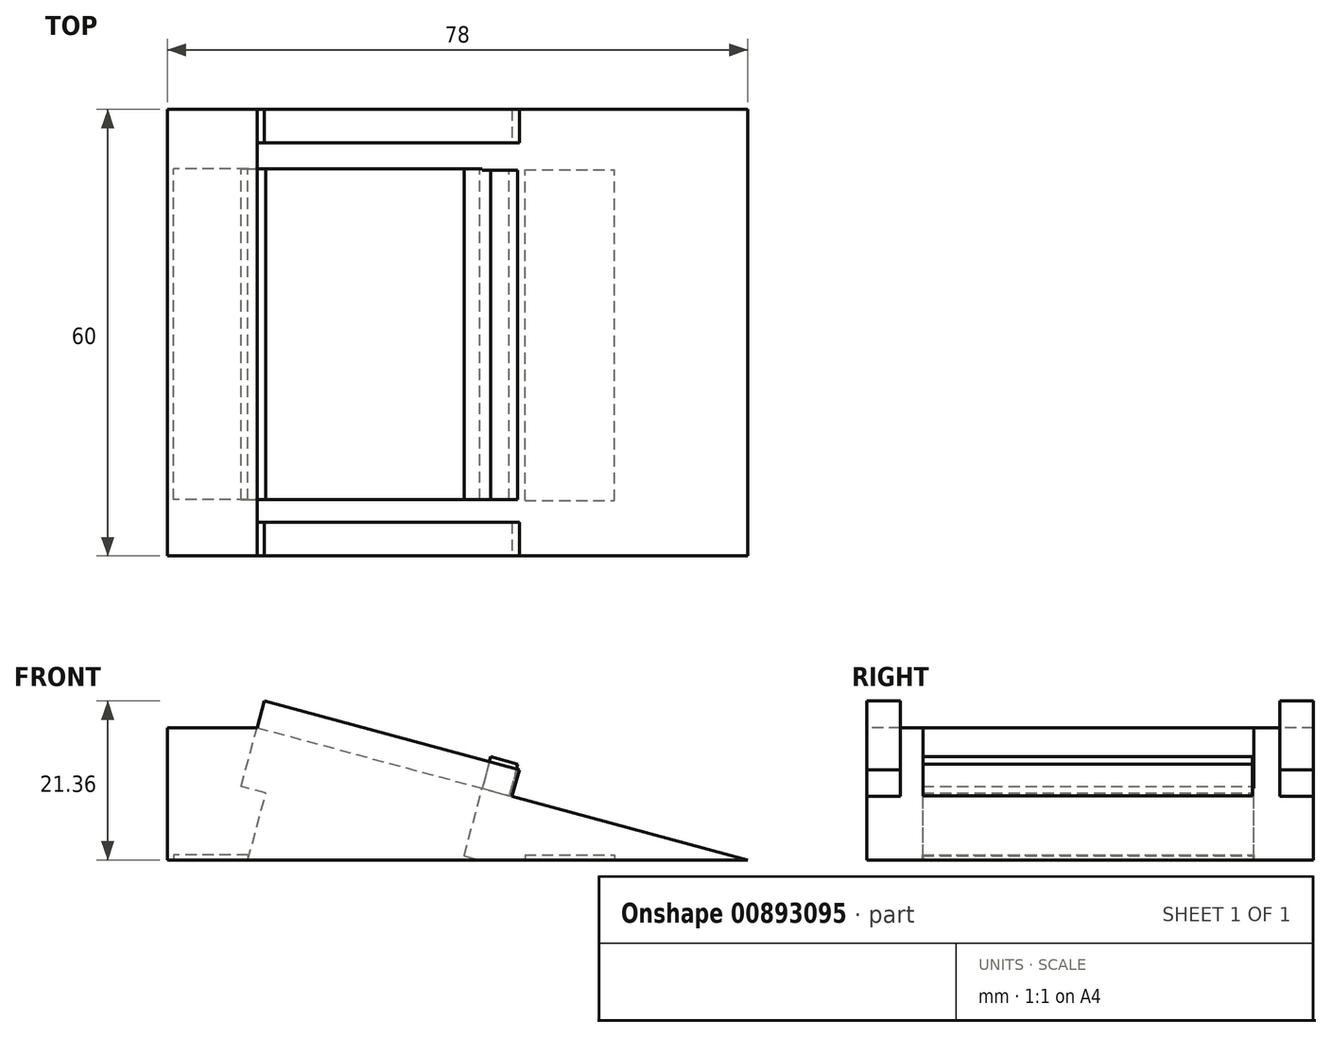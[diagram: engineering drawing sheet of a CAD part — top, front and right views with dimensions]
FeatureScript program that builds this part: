
annotation { "Feature Type Name" : "Feature", "Feature Type Description" : "" }
export const myFeature = defineFeature(function(context is Context, id is Id, definition is map)
    precondition{}
    {
        {
            var Q0;
            Q0=qCreatedBy(makeId("Top.planeOp"),FACE);
            var sketch = newSketch(context, id + "F0", { "sketchPlane" : qUnion([Q0])});
            skLineSegment(sketch, "E0.bottom", {"start": v(-49.5, -60) * mm, "end": v(50.5, -60) * mm});
            skLineSegment(sketch, "E0.top", {"start": v(-49.5, 0) * mm, "end": v(50.5, 0) * mm});
            skLineSegment(sketch, "E0.left", {"start": v(-49.5, -60) * mm, "end": v(-49.5, 0) * mm});
            skLineSegment(sketch, "E0.right", {"start": v(50.5, -60) * mm, "end": v(50.5, 0) * mm});
            skSolve(sketch);
        }
        {
            var Q0;
            Q0=makeQuery(id+"F0.imprint","IMPRINT",FACE,{"disambiguationData":[TD([[makeQuery(id+"F0.imprint","IMPRINT",EDGE,{"derivedFrom":sQuery(id+"F0.wireOp",EDGE,"E0.bottom")}),1.0]])]});
            extrude(context, id + "F1", {"entities" : qUnion([Q0]), "depth" : 31 * mm, "offsetDistance" : 25 * mm});
        }
        {
            var Q0;
            Q0=makeQuery(id+"F1.opExtrude","SWEPT_FACE",FACE,{"disambiguationData":[OSD([sQuery(id+"F0.wireOp",EDGE,"E0.bottom")])]});
            var sketch = newSketch(context, id + "F2", { "sketchPlane" : qUnion([Q0])});
            skLineSegment(sketch, "E1", {"start": v(50.5, 0) * mm, "end": v(-49.5, 26.98) * mm});
            skLineSegment(sketch, "E2", {"start": v(-49.5, 26.98) * mm, "end": v(-49.5, 31) * mm});
            skLineSegment(sketch, "E3", {"start": v(-49.5, 31) * mm, "end": v(50.5, 31) * mm});
            skLineSegment(sketch, "E4", {"start": v(50.5, 31) * mm, "end": v(50.5, 0) * mm});
            skSolve(sketch);
        }
        {
            var Q0;
            Q0 = qSketchRegion(id + "F2", true);
            extrude(context, id + "F3", {"entities" : qUnion([Q0]), "operationType" : NewBodyOperationType.REMOVE, "endBound" : BoundingType.THROUGH_ALL, "oppositeDirection" : true, "depth" : 25 * mm, "offsetDistance" : 25 * mm});
        }
        {
            var Q0;
            Q0=makeQuery(id+"F3.boolean.opBoolean","COPY",FACE,{"derivedFrom":makeQuery(id+"F3.opExtrude","SWEPT_FACE",FACE,{"disambiguationData":[OSD([sQuery(id+"F2.wireOp",EDGE,"E1")])]})});
            var sketch = newSketch(context, id + "F4", { "sketchPlane" : qUnion([Q0])});
            skLineSegment(sketch, "E5.bottom", {"start": v(-16.1, -52.45) * mm, "end": v(14, -52.45) * mm});
            skLineSegment(sketch, "E5.top", {"start": v(-16.1, -8) * mm, "end": v(14, -8) * mm});
            skLineSegment(sketch, "E5.left", {"start": v(-16.1, -52.45) * mm, "end": v(-16.1, -8) * mm});
            skLineSegment(sketch, "E5.right", {"start": v(14, -52.45) * mm, "end": v(14, -8) * mm});
            skSolve(sketch);
        }
        {
            var Q0;
            Q0=makeQuery(id+"F4.imprint","IMPRINT",FACE,{"disambiguationData":[TD([[makeQuery(id+"F4.imprint","IMPRINT",EDGE,{"derivedFrom":sQuery(id+"F4.wireOp",EDGE,"E5.bottom")}),1.0]])]});
            extrude(context, id + "F5", {"entities" : qUnion([Q0]), "operationType" : NewBodyOperationType.REMOVE, "endBound" : BoundingType.THROUGH_ALL, "oppositeDirection" : true, "depth" : 14.7 * mm, "offsetDistance" : 25 * mm});
        }
        {
            var Q0;
            Q0=makeQuery(id+"F3.boolean.opBoolean","COPY",FACE,{"derivedFrom":makeQuery(id+"F3.opExtrude","SWEPT_FACE",FACE,{"disambiguationData":[OSD([sQuery(id+"F2.wireOp",EDGE,"E1")])]})});
            var sketch = newSketch(context, id + "F6", { "sketchPlane" : qUnion([Q0])});
            skLineSegment(sketch, "E6.bottom", {"start": v(-16.1, -52.45) * mm, "end": v(-19.53, -52.45) * mm});
            skLineSegment(sketch, "E6.top", {"start": v(-16.1, -8) * mm, "end": v(-19.53, -8) * mm});
            skLineSegment(sketch, "E6.left", {"start": v(-16.1, -52.45) * mm, "end": v(-16.1, -8) * mm});
            skLineSegment(sketch, "E6.right", {"start": v(-19.53, -52.45) * mm, "end": v(-19.53, -8) * mm});
            skSolve(sketch);
        }
        {
            var Q0;
            Q0 = qSketchRegion(id + "F6", true);
            extrude(context, id + "F7", {"entities" : qUnion([Q0]), "operationType" : NewBodyOperationType.REMOVE, "oppositeDirection" : true, "depth" : 8.2 * mm, "offsetDistance" : 25 * mm});
        }
        {
            var Q0;
            Q0=makeQuery(id+"F5.boolean.opBoolean","COPY",FACE,{"derivedFrom":makeQuery(id+"F5.opExtrude","SWEPT_FACE",FACE,{"disambiguationData":[OSD([sQuery(id+"F4.wireOp",EDGE,"E5.right")])]})});
            extrude(context, id + "F8", {"entities" : qUnion([Q0]), "operationType" : NewBodyOperationType.ADD, "depth" : 2.2 * mm, "offsetDistance" : 25 * mm});
        }
        {
            var Q0;
            Q0=makeQuery(id+"F1.opExtrude","SWEPT_FACE",FACE,{"disambiguationData":[OSD([sQuery(id+"F0.wireOp",EDGE,"E0.left")])]});
            extrude(context, id + "F9", {"entities" : qUnion([Q0]), "operationType" : NewBodyOperationType.REMOVE, "oppositeDirection" : true, "depth" : 22 * mm, "offsetDistance" : 25 * mm});
        }
        {
            var Q0;
            Q0=makeQuery(id+"F8.boolean.opBoolean","MERGE",FACE,{"derivedFrom":[makeQuery(id+"F3.boolean.opBoolean","COPY",FACE,{"derivedFrom":makeQuery(id+"F3.opExtrude","SWEPT_FACE",FACE,{"disambiguationData":[OSD([sQuery(id+"F2.wireOp",EDGE,"E1")])]})}),makeQuery(id+"F8.opExtrude","SWEPT_FACE",FACE,{"disambiguationData":[OSD([sQuery(id+"F4.wireOp",EDGE,"E5.right")])]})]});
            var sketch = newSketch(context, id + "F10", { "sketchPlane" : qUnion([Q0])});
            skLineSegment(sketch, "E7.bottom", {"start": v(11.8, -52.45) * mm, "end": v(15.57, -52.45) * mm});
            skLineSegment(sketch, "E7.top", {"start": v(11.8, -8.16) * mm, "end": v(15.57, -8.16) * mm});
            skLineSegment(sketch, "E7.left", {"start": v(11.8, -52.45) * mm, "end": v(11.8, -8.16) * mm});
            skLineSegment(sketch, "E7.right", {"start": v(15.57, -52.45) * mm, "end": v(15.57, -8.16) * mm});
            skSolve(sketch);
        }
        {
            var Q0;
            Q0=makeQuery(id+"F10.imprint","IMPRINT",FACE,{"disambiguationData":[TD([[makeQuery(id+"F10.imprint","IMPRINT",EDGE,{"derivedFrom":sQuery(id+"F10.wireOp",EDGE,"E7.bottom")}),1.0]])]});
            extrude(context, id + "F11", {"entities" : qUnion([Q0]), "operationType" : NewBodyOperationType.ADD, "depth" : 3.6 * mm, "offsetDistance" : 25 * mm});
        }
        {
            var Q0;
            Q0=makeQuery(id+"F8.boolean.opBoolean","MERGE",FACE,{"derivedFrom":[makeQuery(id+"F3.boolean.opBoolean","COPY",FACE,{"derivedFrom":makeQuery(id+"F3.opExtrude","SWEPT_FACE",FACE,{"disambiguationData":[OSD([sQuery(id+"F2.wireOp",EDGE,"E1")])]})}),makeQuery(id+"F8.opExtrude","SWEPT_FACE",FACE,{"disambiguationData":[OSD([sQuery(id+"F4.wireOp",EDGE,"E5.right")])]})]});
            var sketch = newSketch(context, id + "F12", { "sketchPlane" : qUnion([Q0])});
            skLineSegment(sketch, "E8.bottom", {"start": v(-19.53, 0) * mm, "end": v(15.97, 0) * mm});
            skLineSegment(sketch, "E8.top", {"start": v(-19.53, -4.5) * mm, "end": v(15.97, -4.5) * mm});
            skLineSegment(sketch, "E8.left", {"start": v(-19.53, 0) * mm, "end": v(-19.53, -4.5) * mm});
            skLineSegment(sketch, "E8.right", {"start": v(15.97, 0) * mm, "end": v(15.97, -4.5) * mm});
            skLineSegment(sketch, "E9.bottom", {"start": v(-19.53, -55.5) * mm, "end": v(15.97, -55.5) * mm});
            skLineSegment(sketch, "E9.top", {"start": v(-19.53, -60) * mm, "end": v(15.97, -60) * mm});
            skLineSegment(sketch, "E9.left", {"start": v(-19.53, -55.5) * mm, "end": v(-19.53, -60) * mm});
            skLineSegment(sketch, "E9.right", {"start": v(15.97, -55.5) * mm, "end": v(15.97, -60) * mm});
            skSolve(sketch);
        }
        {
            var Q0;
            Q0 = qSketchRegion(id + "F12", true);
            extrude(context, id + "F13", {"entities" : qUnion([Q0]), "operationType" : NewBodyOperationType.ADD, "depth" : 3.7 * mm, "offsetDistance" : 25 * mm});
        }
        {
            var Q0;
            Q0=makeQuery(id+"F11.opExtrude","CAP_FACE",FACE,{"disambiguationData":[OSD([sQuery(id+"F10.wireOp",EDGE,"E7.bottom"),sQuery(id+"F10.wireOp",EDGE,"E7.top"),sQuery(id+"F10.wireOp",EDGE,"E7.left"),sQuery(id+"F10.wireOp",EDGE,"E7.right")])],"isStart":false});
            extrude(context, id + "F14", {"entities" : qUnion([Q0]), "operationType" : NewBodyOperationType.ADD, "depth" : 0.8 * mm, "offsetDistance" : 25 * mm});
        }
        {
            var Q0;
            Q0=makeQuery(id+"F1.opExtrude","CAP_FACE",FACE,{"disambiguationData":[OSD([sQuery(id+"F0.wireOp",EDGE,"E0.bottom"),sQuery(id+"F0.wireOp",EDGE,"E0.top"),sQuery(id+"F0.wireOp",EDGE,"E0.left"),sQuery(id+"F0.wireOp",EDGE,"E0.right")])],"isStart":true});
            var sketch = newSketch(context, id + "F15", { "sketchPlane" : qUnion([Q0])});
            skLineSegment(sketch, "E10.bottom", {"start": v(20.57, 52.58) * mm, "end": v(32.57, 52.58) * mm});
            skLineSegment(sketch, "E10.top", {"start": v(20.57, 8.13) * mm, "end": v(32.57, 8.13) * mm});
            skLineSegment(sketch, "E10.left", {"start": v(20.57, 52.58) * mm, "end": v(20.57, 8.13) * mm});
            skLineSegment(sketch, "E10.right", {"start": v(32.57, 52.58) * mm, "end": v(32.57, 8.13) * mm});
            skSolve(sketch);
        }
        {
            var Q0;
            Q0=makeQuery(id+"F15.imprint","IMPRINT",FACE,{"disambiguationData":[TD([[makeQuery(id+"F15.imprint","IMPRINT",EDGE,{"derivedFrom":sQuery(id+"F15.wireOp",EDGE,"E10.bottom")}),-1.0]])]});
            var sketch = newSketch(context, id + "F16", { "sketchPlane" : qUnion([Q0])});
            skSolve(sketch);
        }
        {
            var Q0;
            Q0 = qSketchRegion(id + "F16", true);
            var Q1;
            Q1=makeQuery(id+"F15.imprint","IMPRINT",FACE,{"disambiguationData":[TD([[makeQuery(id+"F15.imprint","IMPRINT",EDGE,{"derivedFrom":sQuery(id+"F15.wireOp",EDGE,"E10.bottom")}),-1.0]])]});
            extrude(context, id + "F17", {"entities" : qUnion([Q0, Q1]), "operationType" : NewBodyOperationType.REMOVE, "oppositeDirection" : true, "depth" : 0.7 * mm, "offsetDistance" : 25 * mm});
        }
        {
            var Q0;
            Q0=makeQuery(id+"F1.opExtrude","CAP_FACE",FACE,{"disambiguationData":[OSD([sQuery(id+"F0.wireOp",EDGE,"E0.bottom"),sQuery(id+"F0.wireOp",EDGE,"E0.top"),sQuery(id+"F0.wireOp",EDGE,"E0.left"),sQuery(id+"F0.wireOp",EDGE,"E0.right")])],"isStart":true});
            var sketch = newSketch(context, id + "F18", { "sketchPlane" : qUnion([Q0])});
            skLineSegment(sketch, "E11.bottom", {"start": v(-16.67, 52.45) * mm, "end": v(-26.67, 52.45) * mm});
            skLineSegment(sketch, "E11.top", {"start": v(-16.67, 8) * mm, "end": v(-26.67, 8) * mm});
            skLineSegment(sketch, "E11.left", {"start": v(-16.67, 52.45) * mm, "end": v(-16.67, 8) * mm});
            skLineSegment(sketch, "E11.right", {"start": v(-26.67, 52.45) * mm, "end": v(-26.67, 8) * mm});
            skSolve(sketch);
        }
        {
            var Q0;
            Q0=makeQuery(id+"F18.imprint","IMPRINT",FACE,{"disambiguationData":[TD([[makeQuery(id+"F18.imprint","IMPRINT",EDGE,{"derivedFrom":sQuery(id+"F18.wireOp",EDGE,"E11.bottom")}),1.0]])]});
            extrude(context, id + "F19", {"entities" : qUnion([Q0]), "operationType" : NewBodyOperationType.REMOVE, "oppositeDirection" : true, "depth" : 0.7 * mm, "offsetDistance" : 25 * mm});
        }
        {
            var Q0;
            Q0=makeQuery(id+"F13.boolean.opBoolean","MERGE",FACE,{"derivedFrom":[makeQuery(id+"F1.opExtrude","SWEPT_FACE",FACE,{"disambiguationData":[OSD([sQuery(id+"F0.wireOp",EDGE,"E0.bottom")])]}),makeQuery(id+"F13.opExtrude","SWEPT_FACE",FACE,{"disambiguationData":[OSD([sQuery(id+"F12.wireOp",EDGE,"E9.top")])]})]});
            var sketch = newSketch(context, id + "F20", { "sketchPlane" : qUnion([Q0])});
            skLineSegment(sketch, "E12", {"start": v(-15.43, 17.79) * mm, "end": v(-27.5, 17.79) * mm});
            skLineSegment(sketch, "E13", {"start": v(-27.5, 17.79) * mm, "end": v(-27.5, 21.05) * mm});
            skLineSegment(sketch, "E14", {"start": v(-27.5, 21.05) * mm, "end": v(-15.43, 17.79) * mm});
            skSolve(sketch);
        }
        {
            var Q0;
            Q0=makeQuery(id+"F20.imprint","IMPRINT",FACE,{"disambiguationData":[TD([[makeQuery(id+"F20.imprint","IMPRINT",EDGE,{"derivedFrom":sQuery(id+"F20.wireOp",EDGE,"E12")}),-1.0]])]});
            extrude(context, id + "F21", {"entities" : qUnion([Q0]), "operationType" : NewBodyOperationType.REMOVE, "oppositeDirection" : true, "depth" : 70.6 * mm, "offsetDistance" : 25 * mm});
        }
    });
